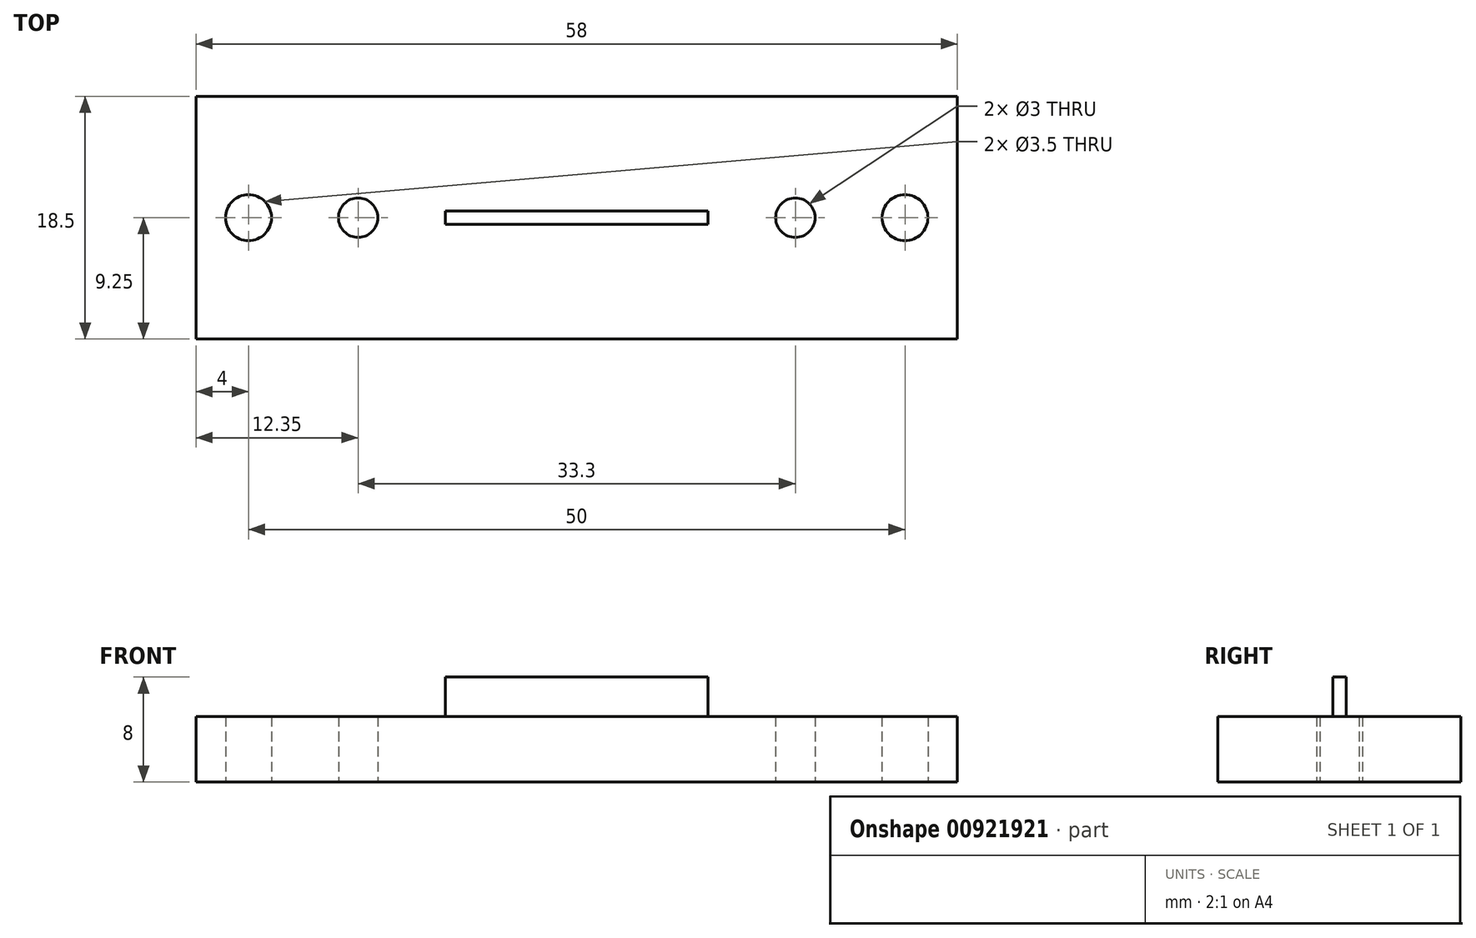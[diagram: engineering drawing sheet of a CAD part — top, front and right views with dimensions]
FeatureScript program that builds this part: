
annotation { "Feature Type Name" : "Feature", "Feature Type Description" : "" }
export const myFeature = defineFeature(function(context is Context, id is Id, definition is map)
    precondition{}
    {
        {
            var Q0;
            Q0=qCreatedBy(makeId("Top.planeOp"),FACE);
            var sketch = newSketch(context, id + "F0", { "sketchPlane" : qUnion([Q0])});
            skLineSegment(sketch, "E0.bottom", {"start": v(19, -9.25) * mm, "end": v(-19, -9.25) * mm});
            skLineSegment(sketch, "E0.top", {"start": v(19, 9.25) * mm, "end": v(-19, 9.25) * mm});
            skLineSegment(sketch, "E0.left", {"start": v(19, -9.25) * mm, "end": v(19, 9.25) * mm});
            skLineSegment(sketch, "E0.right", {"start": v(-19, -9.25) * mm, "end": v(-19, 9.25) * mm});
            skPoint(sketch, "E0.middle", {"position": v(0, 0) * mm});
            skLineSegment(sketch, "E1.bottom", {"start": v(19, -9.25) * mm, "end": v(29, -9.25) * mm});
            skLineSegment(sketch, "E1.top", {"start": v(19, 9.25) * mm, "end": v(29, 9.25) * mm});
            skLineSegment(sketch, "E1.right", {"start": v(29, -9.25) * mm, "end": v(29, 9.25) * mm});
            skLineSegment(sketch, "E2.bottom", {"start": v(-19, -9.25) * mm, "end": v(-29, -9.25) * mm});
            skLineSegment(sketch, "E2.top", {"start": v(-19, 9.25) * mm, "end": v(-29, 9.25) * mm});
            skLineSegment(sketch, "E2.right", {"start": v(-29, -9.25) * mm, "end": v(-29, 9.25) * mm});
            skCircle(sketch, "E3", {"center": v(-25, 0) * mm, "radius": 1.75 * mm});
            skPoint(sketch, "E3.centerSnap0", {"position": v(-29, 0) * mm});
            skCircle(sketch, "E4", {"center": v(25, 0) * mm, "radius": 1.75 * mm});
            skPoint(sketch, "E4.centerSnap0", {"position": v(29, 0) * mm});
            skCircle(sketch, "E5", {"center": v(-16.65, 0) * mm, "radius": 1.5 * mm});
            skCircle(sketch, "E6", {"center": v(16.65, 0) * mm, "radius": 1.5 * mm});
            skSolve(sketch);
        }
        {
            var Q0;
            Q0 = qSketchRegion(id + "F0", true);
            extrude(context, id + "F1", {"entities" : qUnion([Q0]), "depth" : 5 * mm, "offsetDistance" : 25 * mm});
        }
        {
            var Q0;
            Q0=makeQuery(id+"F1.opExtrude","CAP_FACE",FACE,{"disambiguationData":[OSD([sQuery(id+"F0.wireOp",EDGE,"E0.bottom"),sQuery(id+"F0.wireOp",EDGE,"E0.top"),sQuery(id+"F0.wireOp",EDGE,"E1.bottom"),sQuery(id+"F0.wireOp",EDGE,"E1.top"),sQuery(id+"F0.wireOp",EDGE,"E1.right"),sQuery(id+"F0.wireOp",EDGE,"E2.bottom"),sQuery(id+"F0.wireOp",EDGE,"E2.top"),sQuery(id+"F0.wireOp",EDGE,"E2.right"),sQuery(id+"F0.wireOp",EDGE,"E3"),sQuery(id+"F0.wireOp",EDGE,"E4"),sQuery(id+"F0.wireOp",EDGE,"E5"),sQuery(id+"F0.wireOp",EDGE,"E6")])],"isStart":false});
            var sketch = newSketch(context, id + "F2", { "sketchPlane" : qUnion([Q0])});
            skLineSegment(sketch, "E7.bottom", {"start": v(10, 0.5) * mm, "end": v(-10, 0.5) * mm});
            skLineSegment(sketch, "E7.top", {"start": v(10, -0.5) * mm, "end": v(-10, -0.5) * mm});
            skLineSegment(sketch, "E7.left", {"start": v(10, 0.5) * mm, "end": v(10, -0.5) * mm});
            skLineSegment(sketch, "E7.right", {"start": v(-10, 0.5) * mm, "end": v(-10, -0.5) * mm});
            skPoint(sketch, "E7.middle", {"position": v(0, 0) * mm});
            skSolve(sketch);
        }
        {
            var Q0;
            Q0 = qSketchRegion(id + "F2", true);
            extrude(context, id + "F3", {"entities" : qUnion([Q0]), "operationType" : NewBodyOperationType.ADD, "depth" : 3 * mm, "offsetDistance" : 25 * mm});
        }
    });
